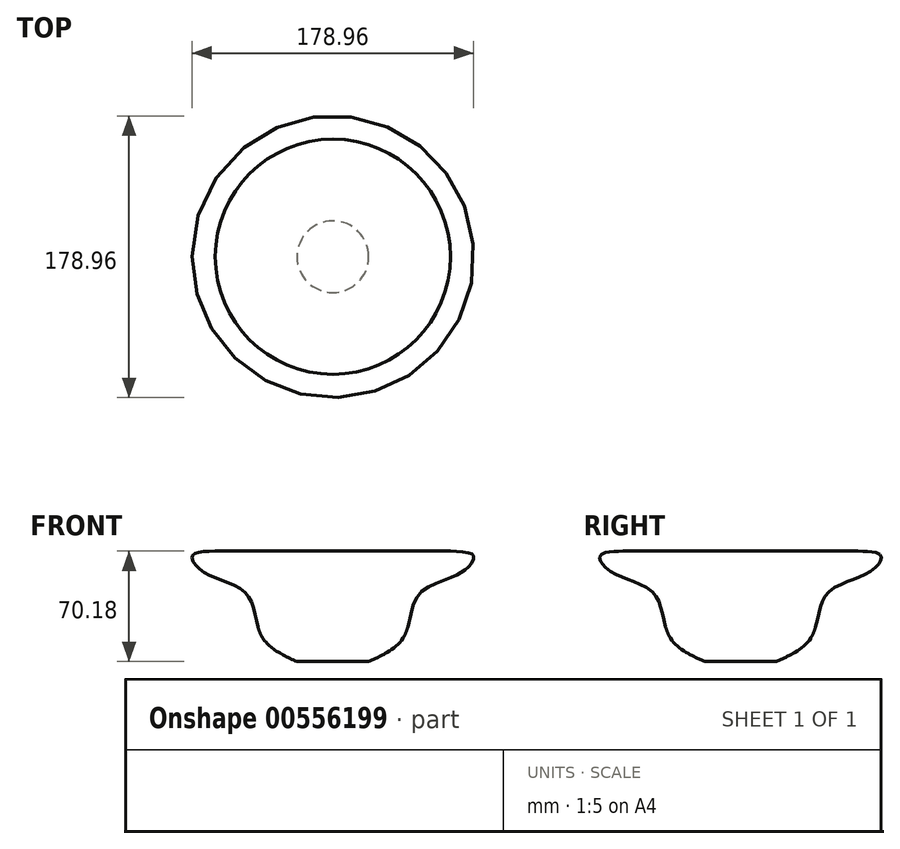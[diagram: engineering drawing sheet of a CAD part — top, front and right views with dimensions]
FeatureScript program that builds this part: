
annotation { "Feature Type Name" : "Feature", "Feature Type Description" : "" }
export const myFeature = defineFeature(function(context is Context, id is Id, definition is map)
    precondition{}
    {
        {
            var Q0;
            Q0=qCreatedBy(makeId("Front.planeOp"),FACE);
            var sketch = newSketch(context, id + "F0", { "sketchPlane" : qUnion([Q0])});
            skLineSegment(sketch, "E0", {"start": v(0, 0) * mm, "end": v(22.74, 0) * mm});
            skLineSegment(sketch, "E1", {"start": v(0, 0) * mm, "end": v(0, 70.18) * mm});
            skLineSegment(sketch, "E2", {"start": v(0, 70.18) * mm, "end": v(74.68, 70.18) * mm});
            skFitSpline(sketch, "E3", {"points": [v(22.74, 0) * mm, v(45.32, 16.3) * mm, v(54.71, 42.83) * mm, v(81.51, 56.64) * mm, v(89.25, 67.14) * mm, v(74.68, 70.18) * mm], "startDerivative": vector(122.42, 56.05) * mm, "endDerivative": vector(-121.7, 3.3) * mm});
            skArc(sketch, "E4", {"start": v(44.55, 15) * mm, "mid": v(51.27, 16.33) * mm, "end": v(47.6, 22.11) * mm});
            skSolve(sketch);
        }
        {
            var Q0;
            Q0=makeQuery(id+"F0.imprint","IMPRINT",FACE,{"disambiguationData":[TD([[makeQuery(id+"F0.imprint","IMPRINT",EDGE,{"derivedFrom":sQuery(id+"F0.wireOp",EDGE,"E0")}),1.0]])]});
            var Q1;
            Q1=sQuery(id+"F0.wireOp",EDGE,"E1");
            revolve(context, id + "F1", {"entities" : qUnion([Q0]), "axis" : qUnion([Q1]), "revolveType" : RevolveType.FULL});
        }
    });
